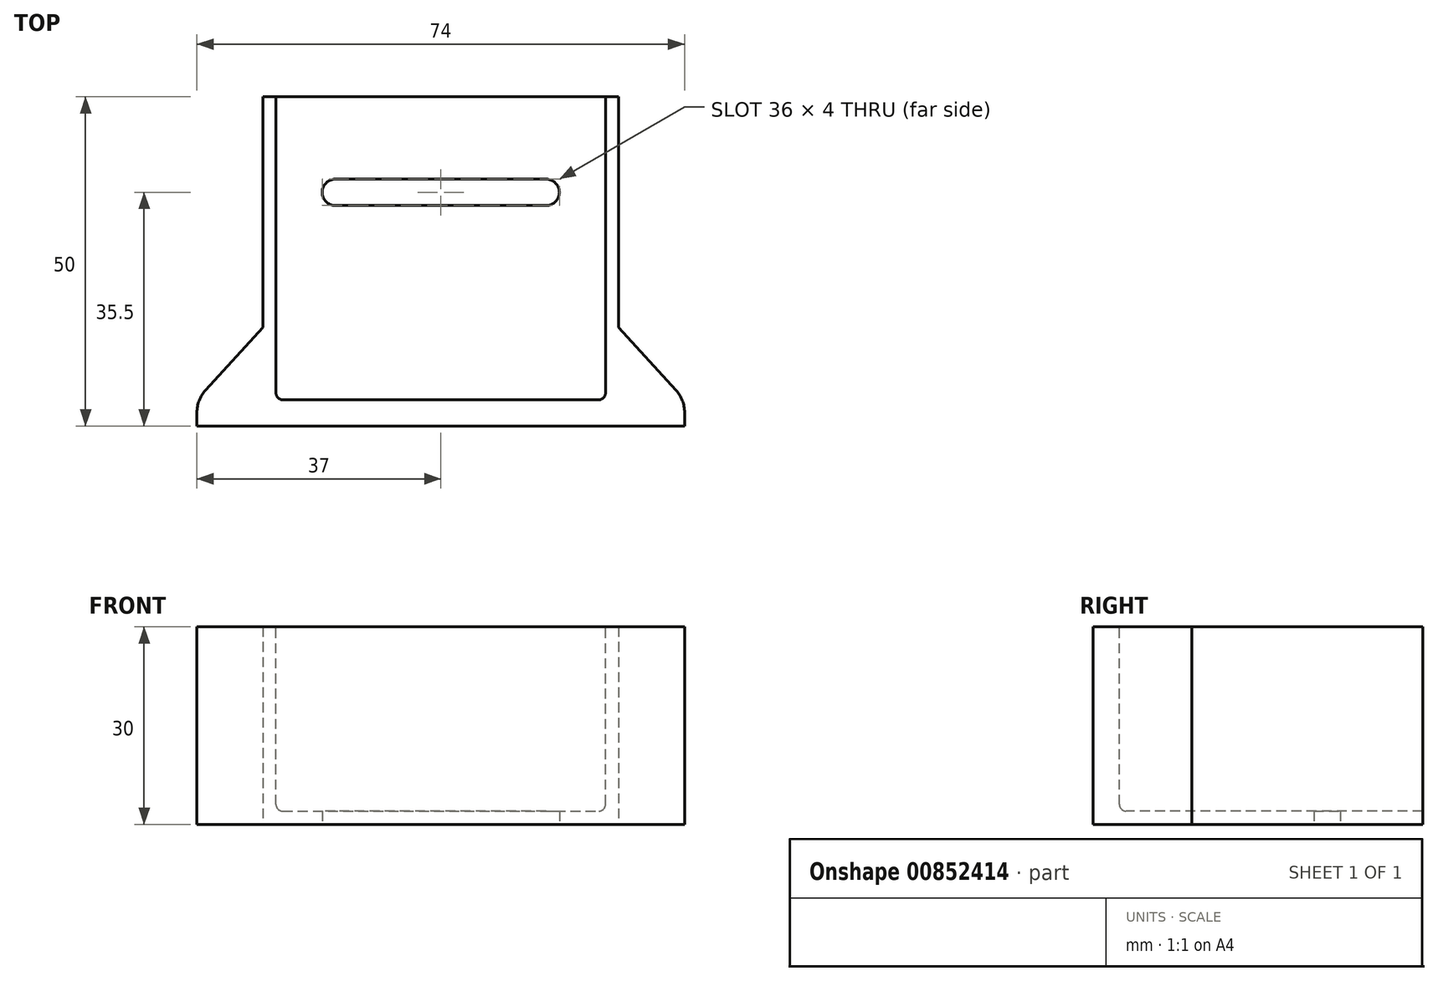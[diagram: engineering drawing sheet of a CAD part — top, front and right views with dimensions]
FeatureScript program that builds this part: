
annotation { "Feature Type Name" : "Feature", "Feature Type Description" : "" }
export const myFeature = defineFeature(function(context is Context, id is Id, definition is map)
    precondition{}
    {
        {
            var Q0;
            Q0=qCreatedBy(makeId("Top.planeOp"),FACE);
            var sketch = newSketch(context, id + "F0", { "sketchPlane" : qUnion([Q0])});
            skLineSegment(sketch, "E0.bottom", {"start": v(-27, 25) * mm, "end": v(27, 25) * mm});
            skLineSegment(sketch, "E0.top", {"start": v(-27, -25) * mm, "end": v(27, -25) * mm});
            skLineSegment(sketch, "E0.left", {"start": v(-27, 25) * mm, "end": v(-27, -25) * mm});
            skLineSegment(sketch, "E0.right", {"start": v(27, 25) * mm, "end": v(27, -25) * mm});
            skSolve(sketch);
        }
        {
            var Q0;
            Q0 = qSketchRegion(id + "F0", true);
            extrude(context, id + "F1", {"entities" : qUnion([Q0]), "depth" : 30 * mm, "offsetDistance" : 25 * mm});
        }
        {
            var Q0;
            Q0=makeQuery(id+"F1.opExtrude","CAP_FACE",FACE,{"disambiguationData":[OSD([sQuery(id+"F0.wireOp",EDGE,"E0.bottom"),sQuery(id+"F0.wireOp",EDGE,"E0.top"),sQuery(id+"F0.wireOp",EDGE,"E0.left"),sQuery(id+"F0.wireOp",EDGE,"E0.right")])],"isStart":false});
            var sketch = newSketch(context, id + "F2", { "sketchPlane" : qUnion([Q0])});
            skLineSegment(sketch, "E1.0", {"start": v(-25, 25) * mm, "end": v(-25, -21) * mm});
            skLineSegment(sketch, "E2.0", {"start": v(25, 25) * mm, "end": v(25, -21) * mm});
            skLineSegment(sketch, "E3.0", {"start": v(-25, -21) * mm, "end": v(25, -21) * mm});
            skLineSegment(sketch, "E4", {"start": v(-25, 25) * mm, "end": v(25, 25) * mm});
            skSolve(sketch);
        }
        {
            var Q0;
            Q0 = qSketchRegion(id + "F2", true);
            extrude(context, id + "F3", {"entities" : qUnion([Q0]), "operationType" : NewBodyOperationType.REMOVE, "oppositeDirection" : true, "depth" : 28 * mm, "offsetDistance" : 25 * mm});
        }
        {
            var Q0;
            Q0=makeQuery(id+"F1.opExtrude","CAP_FACE",FACE,{"disambiguationData":[OSD([sQuery(id+"F0.wireOp",EDGE,"E0.bottom"),sQuery(id+"F0.wireOp",EDGE,"E0.top"),sQuery(id+"F0.wireOp",EDGE,"E0.left"),sQuery(id+"F0.wireOp",EDGE,"E0.right")])],"isStart":false});
            var sketch = newSketch(context, id + "F4", { "sketchPlane" : qUnion([Q0])});
            skLineSegment(sketch, "E5", {"start": v(-27, -25) * mm, "end": v(-37, -25) * mm});
            skLineSegment(sketch, "E6", {"start": v(-37, -25) * mm, "end": v(-37, -21) * mm});
            skLineSegment(sketch, "E7", {"start": v(-37, -21) * mm, "end": v(-27, -10) * mm});
            skLineSegment(sketch, "E8", {"start": v(-27, -10) * mm, "end": v(-27, -25) * mm});
            skLineSegment(sketch, "E9.MirrorCS", {"start": v(37, -25) * mm, "end": v(37, -21) * mm});
            skLineSegment(sketch, "E10.MirrorCS", {"start": v(27, -25) * mm, "end": v(37, -25) * mm});
            skLineSegment(sketch, "E11.MirrorCS", {"start": v(27, -10) * mm, "end": v(27, -25) * mm});
            skLineSegment(sketch, "E12.MirrorCS", {"start": v(37, -21) * mm, "end": v(27, -10) * mm});
            skSolve(sketch);
        }
        {
            var Q0;
            Q0 = qSketchRegion(id + "F4", true);
            var Q1;
            Q1=makeQuery(id+"F1.opExtrude","CAP_FACE",FACE,{"disambiguationData":[OSD([sQuery(id+"F0.wireOp",EDGE,"E0.bottom"),sQuery(id+"F0.wireOp",EDGE,"E0.top"),sQuery(id+"F0.wireOp",EDGE,"E0.left"),sQuery(id+"F0.wireOp",EDGE,"E0.right")])],"isStart":true});
            extrude(context, id + "F5", {"entities" : qUnion([Q0]), "operationType" : NewBodyOperationType.ADD, "endBound" : BoundingType.UP_TO_SURFACE, "oppositeDirection" : true, "depth" : 25 * mm, "endBoundEntityFace" : qUnion([Q1]), "offsetDistance" : 25 * mm});
        }
        {
            var Q0;
            {var subQ0=sQuery(id+"F0.wireOp",EDGE,"E0.right");var subQ1=sQuery(id+"F0.wireOp",EDGE,"E0.left");var subQ2=sQuery(id+"F0.wireOp",EDGE,"E0.top");var subQ3=sQuery(id+"F0.wireOp",EDGE,"E0.bottom");Q0=makeQuery(id+"F5.boolean.opBoolean","MERGE",FACE,{"derivedFrom":[makeQuery(id+"F1.opExtrude","CAP_FACE",FACE,{"disambiguationData":[OSD([subQ3,subQ2,subQ1,subQ0])],"isStart":true}),makeQuery(id+"F5.opExtrude","CAP_FACE",FACE,{"disambiguationData":[OSD([subQ3,subQ2,subQ1,subQ0]),OD(0.0)],"isStart":false}),makeQuery(id+"F5.opExtrude","CAP_FACE",FACE,{"disambiguationData":[OSD([subQ3,subQ2,subQ1,subQ0]),OD(1.0)],"isStart":false})]});}
            var sketch = newSketch(context, id + "F6", { "sketchPlane" : qUnion([Q0])});
            skLineSegment(sketch, "E13", {"start": v(-31.93, -10.5) * mm, "end": v(35.11, -10.5) * mm, "construction": true});
            skLineSegment(sketch, "E14.0", {"start": v(-16, -12.5) * mm, "end": v(16, -12.5) * mm});
            skLineSegment(sketch, "E15.0", {"start": v(-16, -8.5) * mm, "end": v(16, -8.5) * mm});
            skArc(sketch, "E16", {"start": v(16, -12.5) * mm, "mid": v(18, -10.5) * mm, "end": v(16, -8.5) * mm});
            skArc(sketch, "E17", {"start": v(-16, -8.5) * mm, "mid": v(-18, -10.5) * mm, "end": v(-16, -12.5) * mm});
            skSolve(sketch);
        }
        {
            var Q0;
            Q0 = qSketchRegion(id + "F6", true);
            extrude(context, id + "F7", {"entities" : qUnion([Q0]), "operationType" : NewBodyOperationType.REMOVE, "endBound" : BoundingType.THROUGH_ALL, "oppositeDirection" : true, "depth" : 25 * mm, "offsetDistance" : 25 * mm});
        }
        {
            var Q0;
            Q0=makeQuery(id+"F5.opExtrude","SWEPT_EDGE",EDGE,{"disambiguationData":[OSD([sQuery(id+"F0.wireOp",EDGE,"E0.left"),sQuery(id+"F4.wireOp",EDGE,"E7"),sQuery(id+"F4.wireOp",EDGE,"E8")])]});
            var Q1;
            Q1=makeQuery(id+"F5.opExtrude","SWEPT_EDGE",EDGE,{"disambiguationData":[OSD([sQuery(id+"F4.wireOp",EDGE,"E6"),sQuery(id+"F4.wireOp",EDGE,"E7")])]});
            var Q2;
            Q2=makeQuery(id+"F5.opExtrude","SWEPT_EDGE",EDGE,{"disambiguationData":[OSD([sQuery(id+"F0.wireOp",EDGE,"E0.right"),sQuery(id+"F4.wireOp",EDGE,"E11.MirrorCS"),sQuery(id+"F4.wireOp",EDGE,"E12.MirrorCS")])]});
            var Q3;
            Q3=makeQuery(id+"F5.opExtrude","SWEPT_EDGE",EDGE,{"disambiguationData":[OSD([sQuery(id+"F4.wireOp",EDGE,"E9.MirrorCS"),sQuery(id+"F4.wireOp",EDGE,"E12.MirrorCS")])]});
            fillet(context, id + "F8", {"entities" : qUnion([Q0, Q1, Q2, Q3]), "radius" : 5 * mm, "tangentPropagation" : true, "allowEdgeOverflow" : false});
        }
        {
            var Q0;
            Q0=makeQuery(id+"F3.boolean.opBoolean","COPY",EDGE,{"derivedFrom":makeQuery(id+"F3.opExtrude","CAP_EDGE",EDGE,{"disambiguationData":[OSD([sQuery(id+"F2.wireOp",EDGE,"E1.0")])],"isStart":false})});
            var Q1;
            Q1=makeQuery(id+"F3.boolean.opBoolean","COPY",EDGE,{"derivedFrom":makeQuery(id+"F3.opExtrude","CAP_EDGE",EDGE,{"disambiguationData":[OSD([sQuery(id+"F2.wireOp",EDGE,"E2.0")])],"isStart":false})});
            fillet(context, id + "F9", {"entities" : qUnion([Q0, Q1]), "radius" : 1 * mm, "tangentPropagation" : true, "allowEdgeOverflow" : false});
        }
        {
            var Q0;
            Q0=makeQuery(id+"F3.boolean.opBoolean","COPY",EDGE,{"derivedFrom":makeQuery(id+"F3.opExtrude","SWEPT_EDGE",EDGE,{"disambiguationData":[OSD([sQuery(id+"F2.wireOp",EDGE,"E1.0"),sQuery(id+"F2.wireOp",EDGE,"E3.0")])]})});
            fillet(context, id + "F10", {"entities" : qUnion([Q0]), "radius" : 1 * mm, "tangentPropagation" : true, "allowEdgeOverflow" : false});
        }
    });
